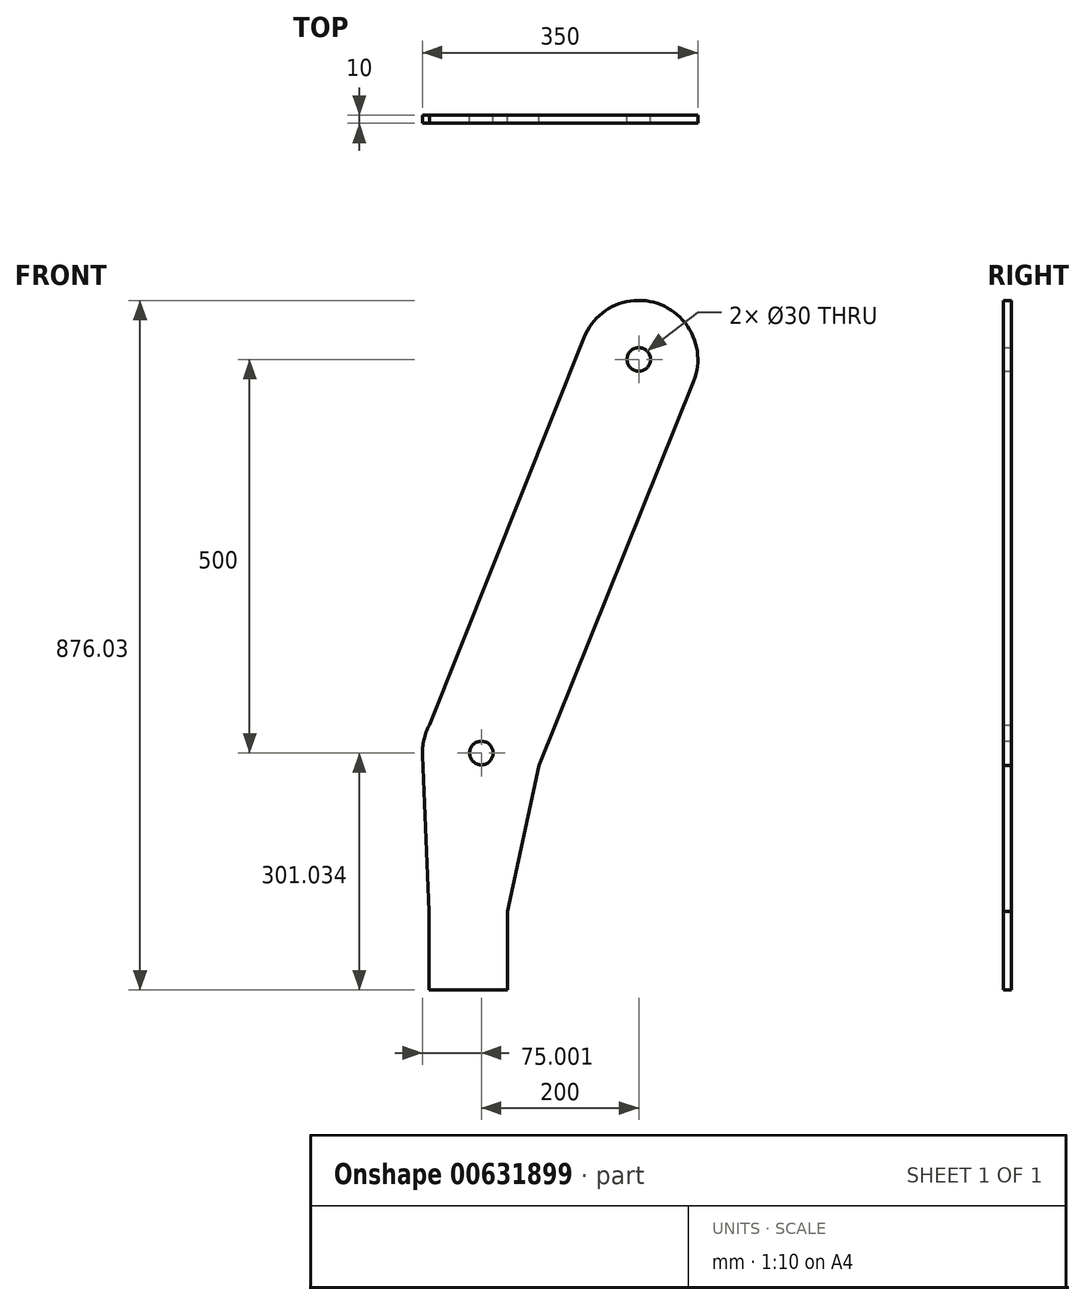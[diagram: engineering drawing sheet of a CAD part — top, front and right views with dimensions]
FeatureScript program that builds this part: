
annotation { "Feature Type Name" : "Feature", "Feature Type Description" : "" }
export const myFeature = defineFeature(function(context is Context, id is Id, definition is map)
    precondition{}
    {
        {
            var Q0;
            Q0=qCreatedBy(makeId("Front.planeOp"),FACE);
            var sketch = newSketch(context, id + "F0", { "sketchPlane" : qUnion([Q0])});
            skLineSegment(sketch, "E0", {"start": v(-416.52, -692.78) * mm, "end": v(-416.52, -792.78) * mm});
            skLineSegment(sketch, "E1", {"start": v(-416.52, -792.78) * mm, "end": v(-316.52, -792.78) * mm});
            skLineSegment(sketch, "E2", {"start": v(-316.52, -792.78) * mm, "end": v(-316.52, -692.78) * mm});
            skLineSegment(sketch, "E3", {"start": v(-416.52, -692.78) * mm, "end": v(-316.52, -692.78) * mm});
            skCircle(sketch, "E4", {"center": v(-149.96, 8.25) * mm, "radius": 75 * mm});
            skCircle(sketch, "E5", {"center": v(-149.96, 8.25) * mm, "radius": 15 * mm});
            skCircle(sketch, "E6", {"center": v(-349.96, -491.75) * mm, "radius": 75 * mm});
            skCircle(sketch, "E7", {"center": v(-349.96, -491.75) * mm, "radius": 15 * mm});
            skLineSegment(sketch, "E8", {"start": v(-416.52, -692.78) * mm, "end": v(-424.9, -494.92) * mm});
            skLineSegment(sketch, "E9", {"start": v(-415.86, -455.94) * mm, "end": v(-219.62, 36.04) * mm});
            skLineSegment(sketch, "E10", {"start": v(-316.52, -692.78) * mm, "end": v(-276.64, -507.53) * mm});
            skLineSegment(sketch, "E11", {"start": v(-276.64, -507.53) * mm, "end": v(-80.38, -19.74) * mm});
            skSolve(sketch);
        }
        {
            var Q0;
            Q0 = qSketchRegion(id + "F0", true);
            var Q1;
            {var subQ0=sQuery(id+"F0.wireOp",EDGE,"E6");var subQ1=sQuery(id+"F0.wireOp",EDGE,"WA19a8Zy-qITi-QStO-RoZA-lV5gnptq3Cfd");var subQ2=makeQuery(id+"F0.imprint","INTERSECT",VERTEX,{"disambiguationData":[OD(0.0)],"derivedFrom":[subQ1,subQ0]});Q1=makeQuery(id+"F0.imprint","IMPRINT",FACE,{"disambiguationData":[TD([[makeQuery(id+"F0.imprint","IMPRINT",EDGE,{"disambiguationData":[TD([[subQ2,-1.0]])],"derivedFrom":subQ1}),1.0]])]});}
            extrude(context, id + "F1", {"entities" : qUnion([Q0, Q1]), "depth" : 10 * mm, "offsetDistance" : 25 * mm});
        }
    });
